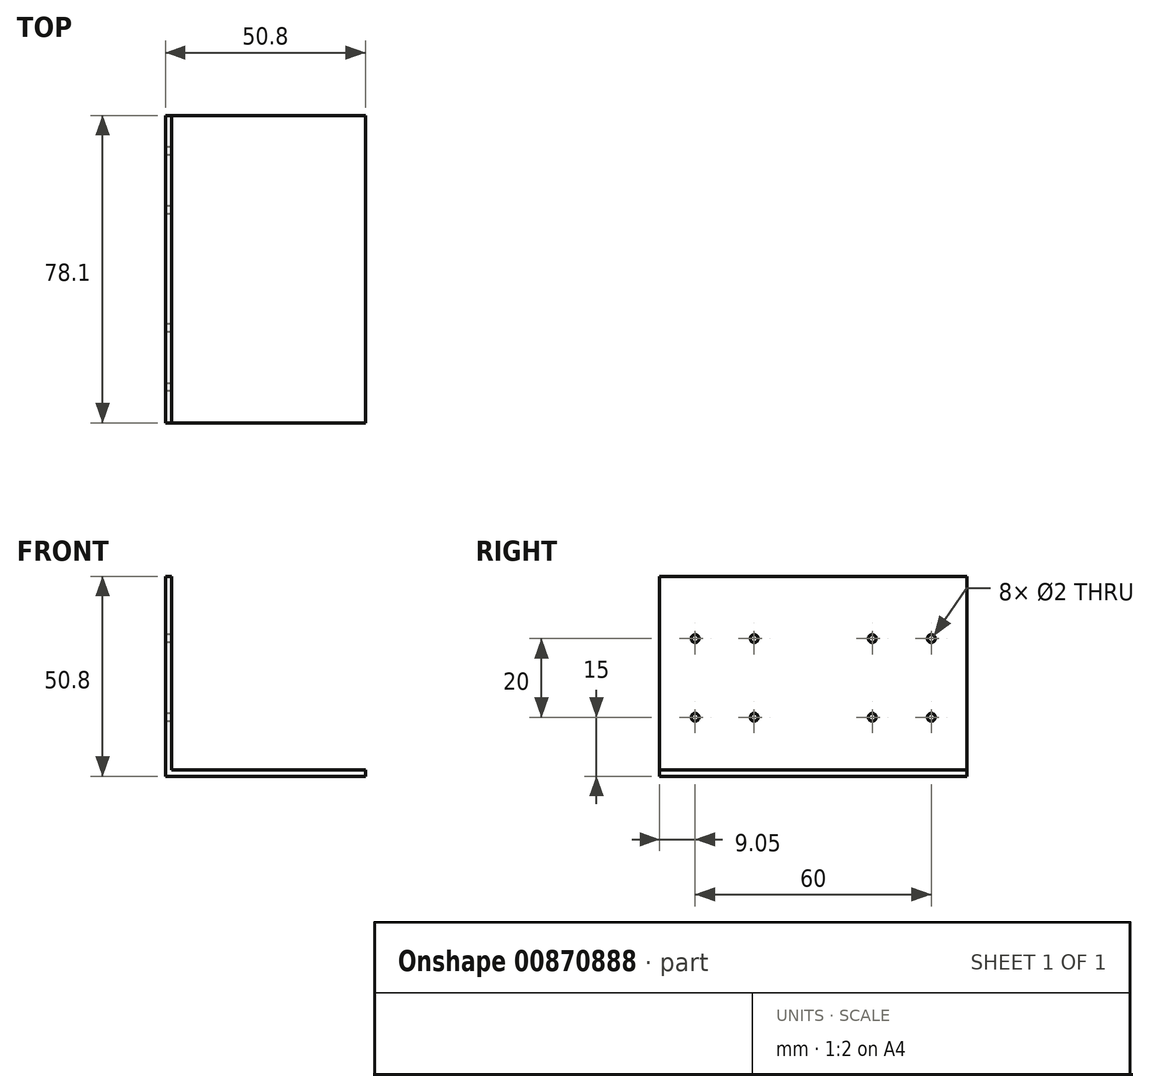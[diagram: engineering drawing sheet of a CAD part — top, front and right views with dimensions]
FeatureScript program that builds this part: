
annotation { "Feature Type Name" : "Feature", "Feature Type Description" : "" }
export const myFeature = defineFeature(function(context is Context, id is Id, definition is map)
    precondition{}
    {
        {
            var Q0;
            Q0=qCreatedBy(makeId("Front.planeOp"),FACE);
            var sketch = newSketch(context, id + "F0", { "sketchPlane" : qUnion([Q0])});
            skLineSegment(sketch, "E0", {"start": v(0, 0) * mm, "end": v(0, 50.8) * mm});
            skLineSegment(sketch, "E1", {"start": v(0, 50.8) * mm, "end": v(1.59, 50.8) * mm});
            skLineSegment(sketch, "E2", {"start": v(1.59, 50.8) * mm, "end": v(1.6, 1.59) * mm});
            skLineSegment(sketch, "E3", {"start": v(1.6, 1.59) * mm, "end": v(50.8, 1.6) * mm});
            skLineSegment(sketch, "E4", {"start": v(50.8, 1.6) * mm, "end": v(50.8, 0) * mm});
            skLineSegment(sketch, "E5", {"start": v(50.8, 0) * mm, "end": v(0, 0) * mm});
            skSolve(sketch);
        }
        {
            var Q0;
            Q0=qSketchRegion(id+"F0",true);
            extrude(context, id + "F1", {"entities" : qUnion([Q0]), "depth" : 78.1 * mm, "offsetDistance" : 25 * mm});
        }
        {
            var Q0;
            Q0=qCreatedBy(makeId("Right.planeOp"),FACE);
            var sketch = newSketch(context, id + "F2", { "sketchPlane" : qUnion([Q0])});
            skPoint(sketch, "E6", {"position": v(-39.05, 0) * mm});
            skPoint(sketch, "E7", {"position": v(-24.05, 15) * mm});
            skPoint(sketch, "E8", {"position": v(-24.05, 35) * mm});
            skPoint(sketch, "E9", {"position": v(-9.05, 35) * mm});
            skPoint(sketch, "E10", {"position": v(-9.05, 15) * mm});
            skPoint(sketch, "E11", {"position": v(-54.05, 15) * mm});
            skPoint(sketch, "E12", {"position": v(-69.05, 15) * mm});
            skPoint(sketch, "E13", {"position": v(-69.05, 35) * mm});
            skPoint(sketch, "E14", {"position": v(-54.05, 35) * mm});
            skCircle(sketch, "E15", {"center": v(-9.05, 15) * mm, "radius": 1 * mm});
            skCircle(sketch, "E16", {"center": v(-9.05, 35) * mm, "radius": 1 * mm});
            skCircle(sketch, "E17", {"center": v(-24.05, 35) * mm, "radius": 1 * mm});
            skCircle(sketch, "E18", {"center": v(-24.05, 15) * mm, "radius": 1 * mm});
            skCircle(sketch, "E19", {"center": v(-54.05, 15) * mm, "radius": 1 * mm});
            skCircle(sketch, "E20", {"center": v(-54.05, 35) * mm, "radius": 1 * mm});
            skCircle(sketch, "E21", {"center": v(-69.05, 35) * mm, "radius": 1 * mm});
            skCircle(sketch, "E22", {"center": v(-69.05, 15) * mm, "radius": 1 * mm});
            skSolve(sketch);
        }
        {
            var Q0;
            Q0 = qSketchRegion(id + "F2", true);
            extrude(context, id + "F3", {"entities" : qUnion([Q0]), "operationType" : NewBodyOperationType.REMOVE, "endBound" : BoundingType.THROUGH_ALL, "depth" : 25 * mm, "offsetDistance" : 25 * mm});
        }
    });
